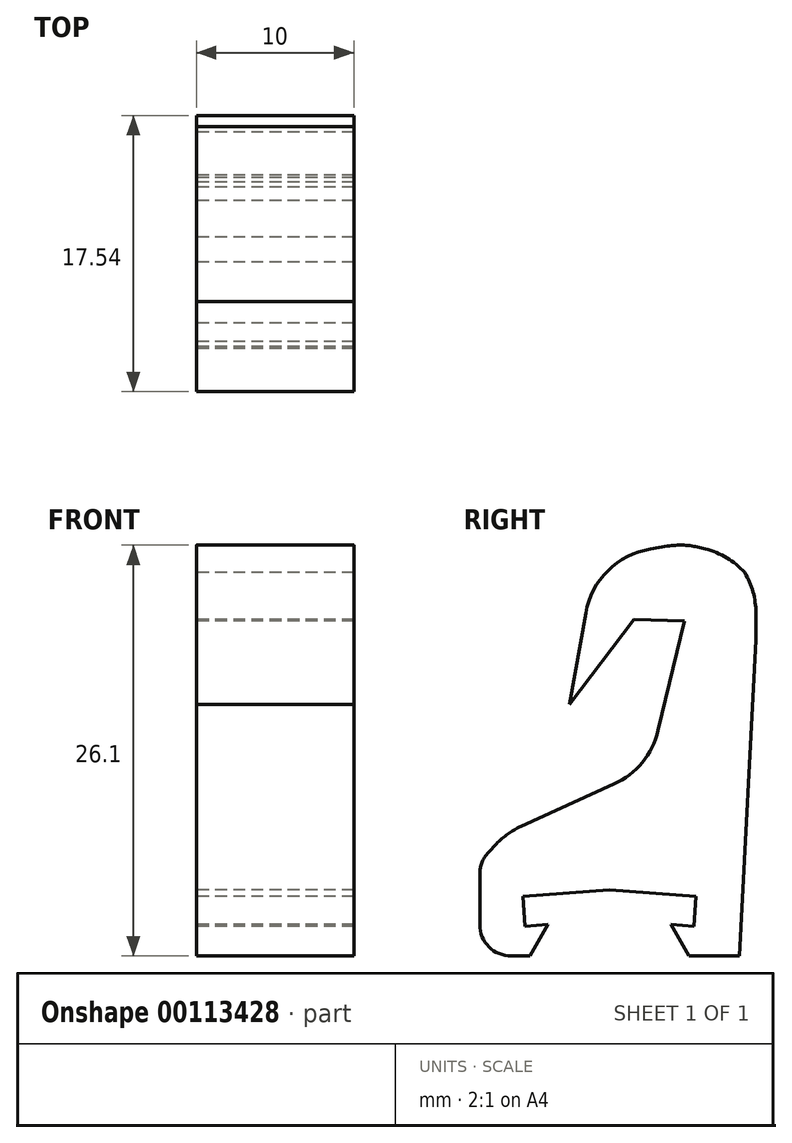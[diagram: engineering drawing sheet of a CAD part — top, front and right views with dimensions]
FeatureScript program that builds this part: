
annotation { "Feature Type Name" : "Feature", "Feature Type Description" : "" }
export const myFeature = defineFeature(function(context is Context, id is Id, definition is map)
    precondition{}
    {
        {
            var Q0;
            Q0=qCreatedBy(makeId("Right.planeOp"),FACE);
            var sketch = newSketch(context, id + "F0", { "sketchPlane" : qUnion([Q0])});
            skLineSegment(sketch, "E0", {"start": v(-7, 0) * mm, "end": v(-3.9, 0) * mm, "construction": true});
            skLineSegment(sketch, "E1", {"start": v(-3.9, 0) * mm, "end": v(-3.9, 2) * mm, "construction": true});
            skLineSegment(sketch, "E2", {"start": v(-3.9, 2) * mm, "end": v(-5, 2) * mm, "construction": true});
            skLineSegment(sketch, "E3", {"start": v(-5, 2) * mm, "end": v(-5, 3.8) * mm, "construction": true});
            skLineSegment(sketch, "E4", {"start": v(-5, 3.8) * mm, "end": v(0, 3.8) * mm, "construction": true});
            skLineSegment(sketch, "E5.MirrorCS", {"start": v(7, 0) * mm, "end": v(3.9, 0) * mm, "construction": true});
            skLineSegment(sketch, "E6.MirrorCS", {"start": v(3.9, 2) * mm, "end": v(5, 2) * mm, "construction": true});
            skLineSegment(sketch, "E7.MirrorCS", {"start": v(5, 3.8) * mm, "end": v(0, 3.8) * mm, "construction": true});
            skLineSegment(sketch, "E8.MirrorCS", {"start": v(3.9, 0) * mm, "end": v(3.9, 2) * mm, "construction": true});
            skLineSegment(sketch, "E9.MirrorCS", {"start": v(5, 2) * mm, "end": v(5, 3.8) * mm, "construction": true});
            skSolve(sketch);
        }
        {
            var Q0;
            Q0=qCreatedBy(makeId("Right.planeOp"),FACE);
            var sketch = newSketch(context, id + "F1", { "sketchPlane" : qUnion([Q0])});
            skLineSegment(sketch, "E10", {"start": v(-3.9, 2) * mm, "end": v(-5.05, 0) * mm});
            skLineSegment(sketch, "E11", {"start": v(-5.05, 0) * mm, "end": v(-8.24, 0) * mm});
            skLineSegment(sketch, "E12", {"start": v(-8.24, 0) * mm, "end": v(-8.24, 6) * mm});
            skLineSegment(sketch, "E13", {"start": v(0, 4.19) * mm, "end": v(-5.5, 3.79) * mm});
            skLineSegment(sketch, "E14", {"start": v(-5.5, 3.79) * mm, "end": v(-5.36, 1.9) * mm});
            skLineSegment(sketch, "E15", {"start": v(-5.36, 1.9) * mm, "end": v(-3.9, 2) * mm});
            skLineSegment(sketch, "E16.MirrorCS", {"start": v(5.36, 1.9) * mm, "end": v(3.9, 2) * mm});
            skLineSegment(sketch, "E17.MirrorCS", {"start": v(5.5, 3.79) * mm, "end": v(5.36, 1.9) * mm});
            skLineSegment(sketch, "E18.MirrorCS", {"start": v(3.9, 2) * mm, "end": v(5.05, 0) * mm});
            skLineSegment(sketch, "E19.MirrorCS", {"start": v(5.05, 0) * mm, "end": v(8.24, 0) * mm});
            skLineSegment(sketch, "E20.MirrorCS", {"start": v(0, 4.19) * mm, "end": v(5.5, 3.79) * mm});
            skLineSegment(sketch, "E21.left", {"start": v(-8.24, 6) * mm, "end": v(-6.51, 7.84) * mm});
            skLineSegment(sketch, "E22", {"start": v(-6.51, 7.84) * mm, "end": v(2.52, 11.94) * mm});
            skLineSegment(sketch, "E23", {"start": v(2.52, 11.94) * mm, "end": v(4.76, 21.27) * mm});
            skLineSegment(sketch, "E24", {"start": v(4.76, 21.27) * mm, "end": v(1.57, 21.4) * mm});
            skLineSegment(sketch, "E25", {"start": v(1.57, 21.4) * mm, "end": v(-2.53, 16) * mm});
            skLineSegment(sketch, "E26", {"start": v(-2.53, 16) * mm, "end": v(-0.89, 25.27) * mm});
            skLineSegment(sketch, "E27", {"start": v(-0.89, 25.27) * mm, "end": v(4.72, 26.2) * mm});
            skLineSegment(sketch, "E28", {"start": v(4.72, 26.2) * mm, "end": v(7.83, 25.42) * mm});
            skLineSegment(sketch, "E29", {"start": v(7.83, 25.42) * mm, "end": v(9.3, 23.43) * mm});
            skLineSegment(sketch, "E30", {"start": v(9.3, 23.43) * mm, "end": v(9.3, 20.22) * mm});
            skLineSegment(sketch, "E31", {"start": v(9.3, 20.22) * mm, "end": v(8.24, 0) * mm});
            skPoint(sketch, "E32.MirrorCS.start.orphan", {"position": v(0, 6.34) * mm});
            skPoint(sketch, "E33.MirrorCS.end.orphan", {"position": v(8.24, 6) * mm});
            skSolve(sketch);
        }
        {
            var Q0;
            Q0=makeQuery(id+"F1.imprint","IMPRINT",FACE,{"disambiguationData":[TD([[makeQuery(id+"F1.imprint","IMPRINT",EDGE,{"derivedFrom":sQuery(id+"F1.wireOp",EDGE,"E10")}),-1.0]])]});
            extrude(context, id + "F2", {"entities" : qUnion([Q0]), "depth" : 10 * mm});
        }
        {
            var Q0;
            Q0=makeQuery(id+"F2.opExtrude","SWEPT_EDGE",EDGE,{"disambiguationData":[OSD([sQuery(id+"F1.wireOp",EDGE,"E30"),sQuery(id+"F1.wireOp",EDGE,"E31")])]});
            var Q1;
            Q1=makeQuery(id+"F2.opExtrude","SWEPT_EDGE",EDGE,{"disambiguationData":[OSD([sQuery(id+"F1.wireOp",EDGE,"E29"),sQuery(id+"F1.wireOp",EDGE,"E30")])]});
            var Q2;
            Q2=makeQuery(id+"F2.opExtrude","SWEPT_EDGE",EDGE,{"disambiguationData":[OSD([sQuery(id+"F1.wireOp",EDGE,"E28"),sQuery(id+"F1.wireOp",EDGE,"E29")])]});
            var Q3;
            Q3=makeQuery(id+"F2.opExtrude","SWEPT_EDGE",EDGE,{"disambiguationData":[OSD([sQuery(id+"F1.wireOp",EDGE,"E27"),sQuery(id+"F1.wireOp",EDGE,"E28")])]});
            var Q4;
            Q4=makeQuery(id+"F2.opExtrude","SWEPT_EDGE",EDGE,{"disambiguationData":[OSD([sQuery(id+"F1.wireOp",EDGE,"E26"),sQuery(id+"F1.wireOp",EDGE,"E27")])]});
            var Q5;
            Q5=makeQuery(id+"F2.opExtrude","SWEPT_EDGE",EDGE,{"disambiguationData":[OSD([sQuery(id+"F1.wireOp",EDGE,"E21.left"),sQuery(id+"F1.wireOp",EDGE,"E22")])]});
            var Q6;
            Q6=makeQuery(id+"F2.opExtrude","SWEPT_EDGE",EDGE,{"disambiguationData":[OSD([sQuery(id+"F1.wireOp",EDGE,"E22"),sQuery(id+"F1.wireOp",EDGE,"E23")])]});
            fillet(context, id + "F3", {"entities" : qUnion([Q0, Q1, Q2, Q3, Q4, Q5, Q6]), "radius" : 5 * mm, "tangentPropagation" : true, "allowEdgeOverflow" : false});
        }
        {
            var Q0;
            Q0=makeQuery(id+"F2.opExtrude","SWEPT_EDGE",EDGE,{"disambiguationData":[OSD([sQuery(id+"F1.wireOp",EDGE,"E11"),sQuery(id+"F1.wireOp",EDGE,"E12")])]});
            var Q1;
            Q1=makeQuery(id+"F2.opExtrude","SWEPT_EDGE",EDGE,{"disambiguationData":[OSD([sQuery(id+"F1.wireOp",EDGE,"E12"),sQuery(id+"F1.wireOp",EDGE,"E21.left")])]});
            fillet(context, id + "F4", {"entities" : qUnion([Q0, Q1]), "radius" : 2 * mm, "tangentPropagation" : true, "allowEdgeOverflow" : false});
        }
    });
